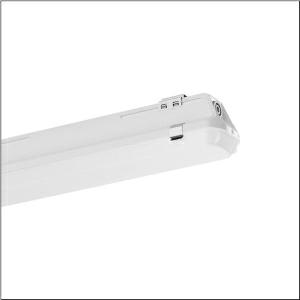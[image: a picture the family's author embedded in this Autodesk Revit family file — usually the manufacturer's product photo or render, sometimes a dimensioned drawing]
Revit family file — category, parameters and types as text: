
# Revit family: monsun_r__11_51fp10dp4b0q_1ef0
name_source: partatom
category: Lighting Fixtures
units: mm (PartAtom-declared; Revit-internal decimal feet)

## family parameters
Cut with Voids When Loaded = No
Host = Face
Light Source = No
Part Type = Normal
Room Calculation Point = No
Round Connector Dimension = Use Diameter
Shared = No

## types (1)
- --- (1 x LED, 12110 lm, 67.6 W, 4000K)
    Apparent Load = 68 VA
    CIE Flux Codes = 47 76 93 94 100
    Color Rendering = 80
    Color Temperature = 4000K
    Default Elevation = 1800 mm
    Description = Monsun® 11, damp-proof luminaire, chain hanger, primary optical cover: enclosure, of PMMA, light emission: direct distribution, primary light characteristic: symmetric, installation type: suspended mounting, surface-mounted, horizontal mounting, vertical mounting, LED, rated luminous flux: 12.110lm, luminous efficacy: 179lm/W, light colour: 840, colour temperature: 4000K, control gear: ECG DALI, with terminal, 5-pole, max. 2.5mm², mains connection: 220..240V, AC, 50/60Hz, rated input power: 68W, luminaire housing, of glass-fibre reinforced polyester, uncoated, bright grey, incl. chain hanger, length: 1.590mm, width: 90mm, height: 88mm, clip for enclosure, of stainless steel (V2A), ceiling mounting element, of stainless steel (V2A), chain hanger, of stainless steel (V2A), protection rating (complete): IP66, insulation class (complete): insulation class I (protective earthing), certification: CE, ENEC, VDE, UKCA, protection symbol: D, impact resistance: IK04, permissible operating ambient temperature: -40..+35°C, standard: EN 50419, EN 60598-2-1, no direct snow, no direct sun, no direct rain, for indoor or canopied outdoor use, corresponds to IFS (International Featured Standards) requirements for safety and quality in the food industry, contact your sales advisor before using the luminaires in applications with unclear chemical exposure, large temperature fluctuations or condensation-forming humidity, LABS conformity tested according to VDMA 24364:2018-05, packaging unit: 1 piece
    Height = 89 mm
    Lamp = 1 x LED
    Lamp Light Flux = 12110 lm
    Lamp Power = 67.6 W
    Lamp count = 1
    Length = 1590 mm
    Luminous efficacy = 179 lm/W
    Manufacturer = Siteco
    ModVariant = No
    Model = 51FP10DP4B0Q
    Mounting Place = Ceiling
    Mounting Type = Surface mounted
    Number of Poles = 1
    OnlyDefault = Yes
    Power Factor = 1
    Product Name = Monsun® 11
    Product group = damp-proof luminaire
    ProductGroupID = 300
    Protection Class = Protection class I
    Protection Degree = IP 66
    RLX_Detail_Level = 1
    RLX_Emergency_Light_Flux = 0 lm
    RLX_Emergency_Type = 0
    RLX_Emergency_Type_DB = No
    RlxData = <blob elided: 92557 chars, md5=b4525d91>
    Socket = socket
    Standby Power = 0 W
    System Light Flux = 12110 lm
    System Power = 68 W
    Type Comments = factory setting: luminous flux: 100 % | dim-lin: 254 | 389 mA
    Type Image = l_1004748.jpg
    URL = http://relux.com
    VarID = @adj_142049
    Voltage = 0 V
    Weight = 0.00 kg
    Width = 90 mm

## geometry (parser evidence)
native form markers: Blend x4, Sweep x13
no freeform markers — native parametric forms only
